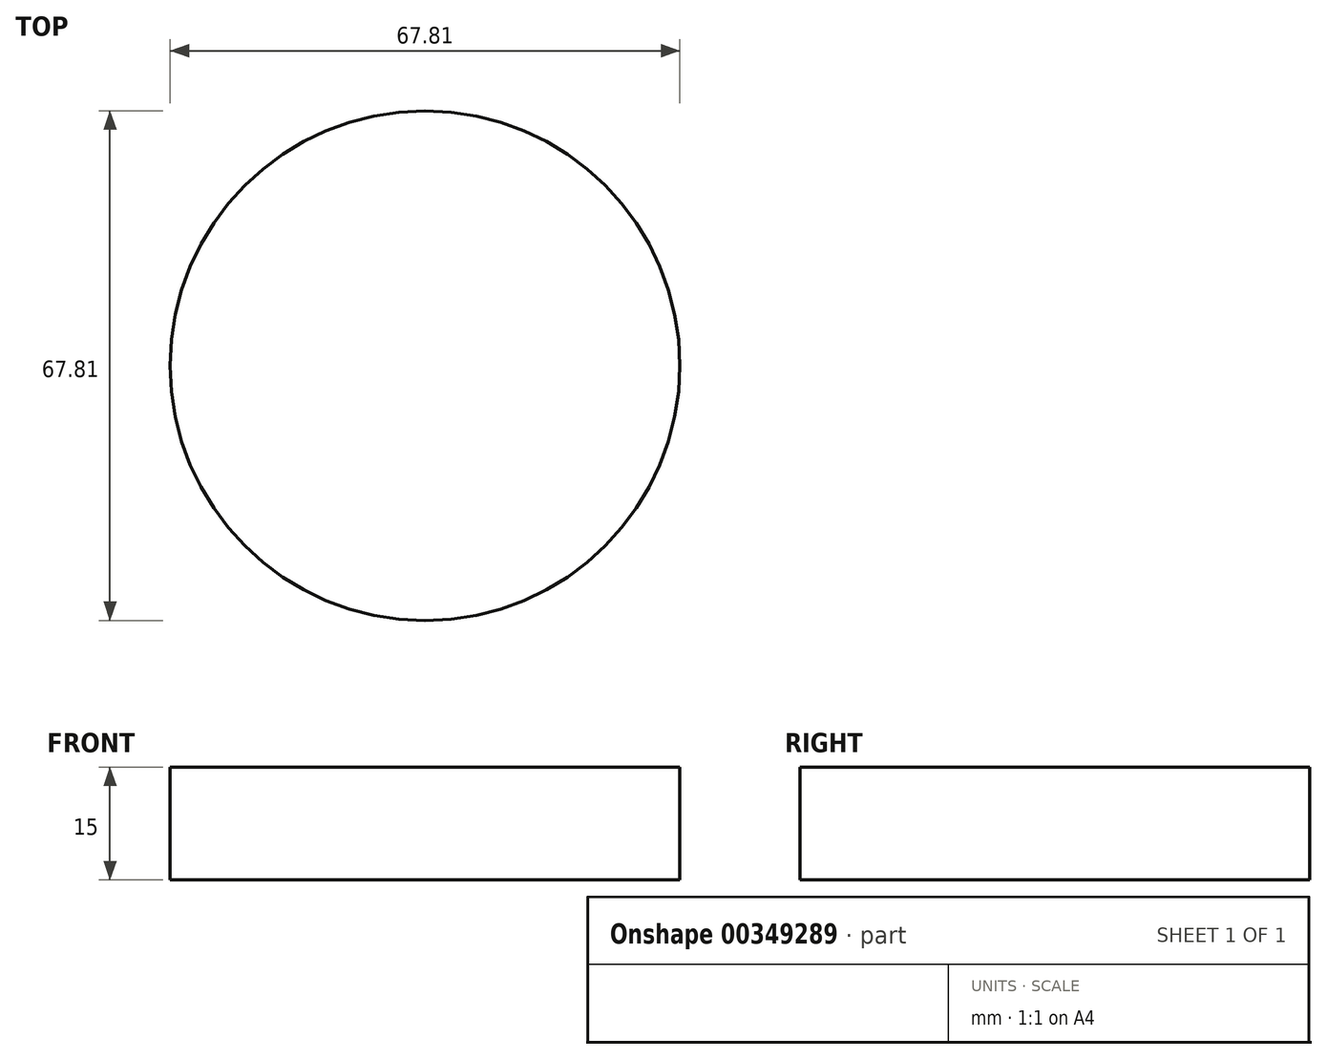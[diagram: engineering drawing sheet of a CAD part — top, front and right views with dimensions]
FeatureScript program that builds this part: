
annotation { "Feature Type Name" : "Feature", "Feature Type Description" : "" }
export const myFeature = defineFeature(function(context is Context, id is Id, definition is map)
    precondition{}
    {
        {
            var Q0;
            Q0=qCreatedBy(makeId("Top.planeOp"),FACE);
            var sketch = newSketch(context, id + "F0", { "sketchPlane" : qUnion([Q0])});
            skCircle(sketch, "E0", {"center": v(-15.05, 16.3) * mm, "radius": 33.9 * mm});
            skSolve(sketch);
        }
        {
            var Q0;
            Q0 = qSketchRegion(id + "F0", true);
            extrude(context, id + "F1", {"entities" : qUnion([Q0]), "depth" : 15 * mm});
        }
        {
            var Q0;
            Q0=makeQuery(id+"F1.opExtrude","CAP_FACE",FACE,{"disambiguationData":[OSD([sQuery(id+"F0.wireOp",EDGE,"E0")])],"isStart":false});
            var sketch = newSketch(context, id + "F2", { "sketchPlane" : qUnion([Q0])});
            skCircle(sketch, "E1", {"center": v(-15.05, 16.3) * mm, "radius": 27.98 * mm});
            skSolve(sketch);
        }
        {
            var Q0;
            Q0=makeQuery(id+"F2.imprint","IMPRINT",FACE,{"disambiguationData":[TD([[makeQuery(id+"F2.imprint","IMPRINT",EDGE,{"derivedFrom":sQuery(id+"F2.wireOp",EDGE,"E1")}),1.0]])]});
            extrude(context, id + "F3", {"entities" : qUnion([Q0]), "operationType" : NewBodyOperationType.ADD, "oppositeDirection" : true, "depth" : 10 * mm});
        }
    });
